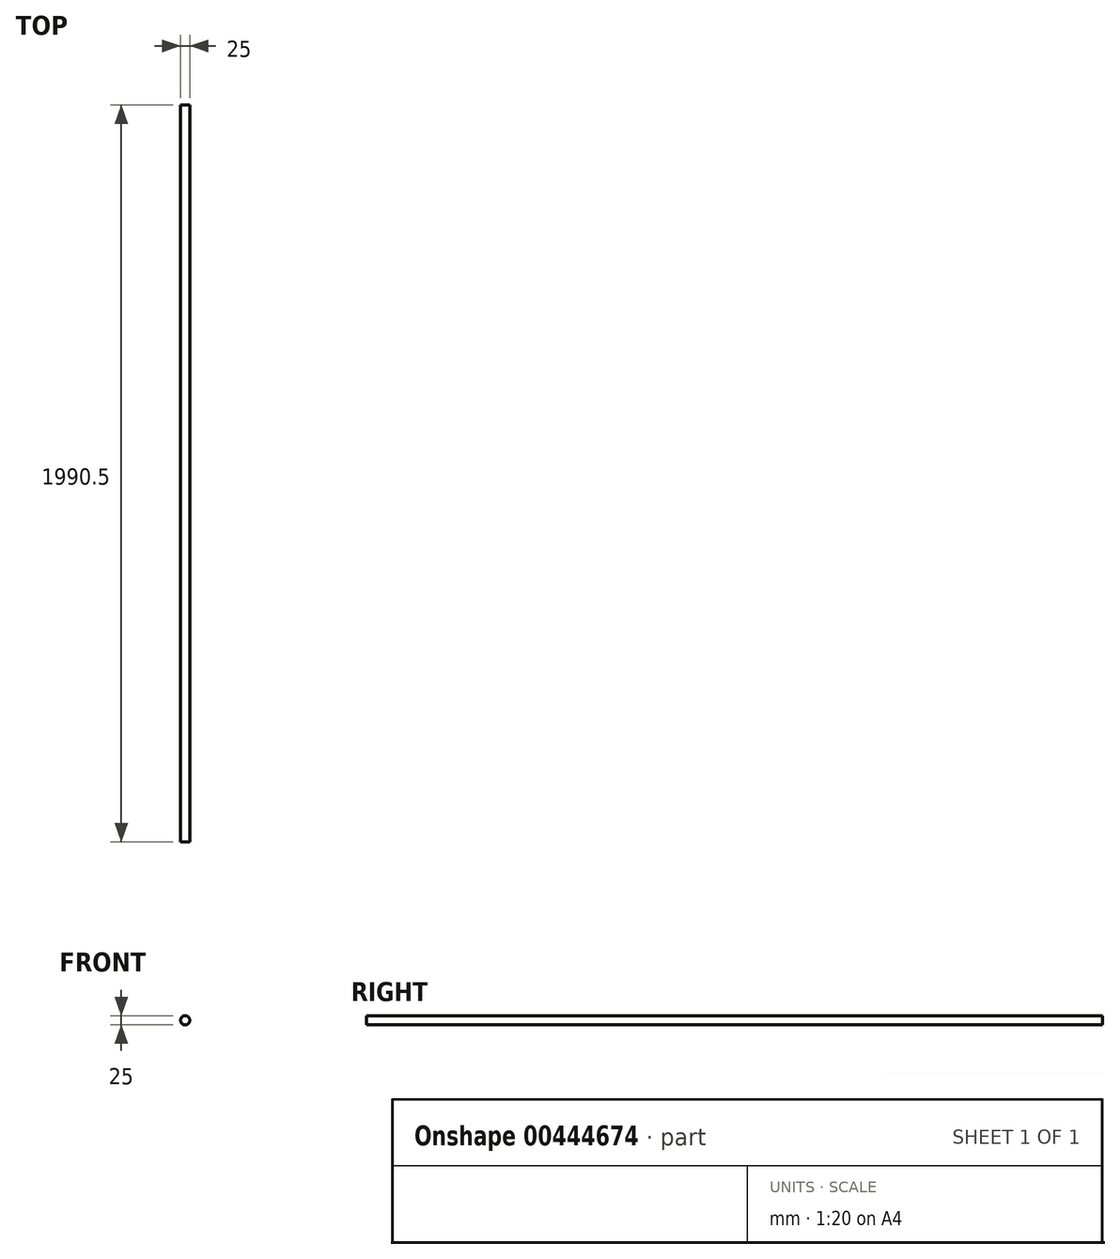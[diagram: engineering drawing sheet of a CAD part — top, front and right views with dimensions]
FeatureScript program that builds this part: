
annotation { "Feature Type Name" : "Feature", "Feature Type Description" : "" }
export const myFeature = defineFeature(function(context is Context, id is Id, definition is map)
    precondition{}
    {
        {
            var Q0;
            Q0=qCreatedBy(makeId("Front.planeOp"),FACE);
            var sketch = newSketch(context, id + "F0", { "sketchPlane" : qUnion([Q0])});
            skCircle(sketch, "E0", {"center": v(48.4, 28.66) * mm, "radius": 12.5 * mm});
            skSolve(sketch);
        }
        {
            var Q0;
            Q0 = qSketchRegion(id + "F0", true);
            extrude(context, id + "F1", {"entities" : qUnion([Q0]), "depth" : 1990.5 * mm});
        }
    });
